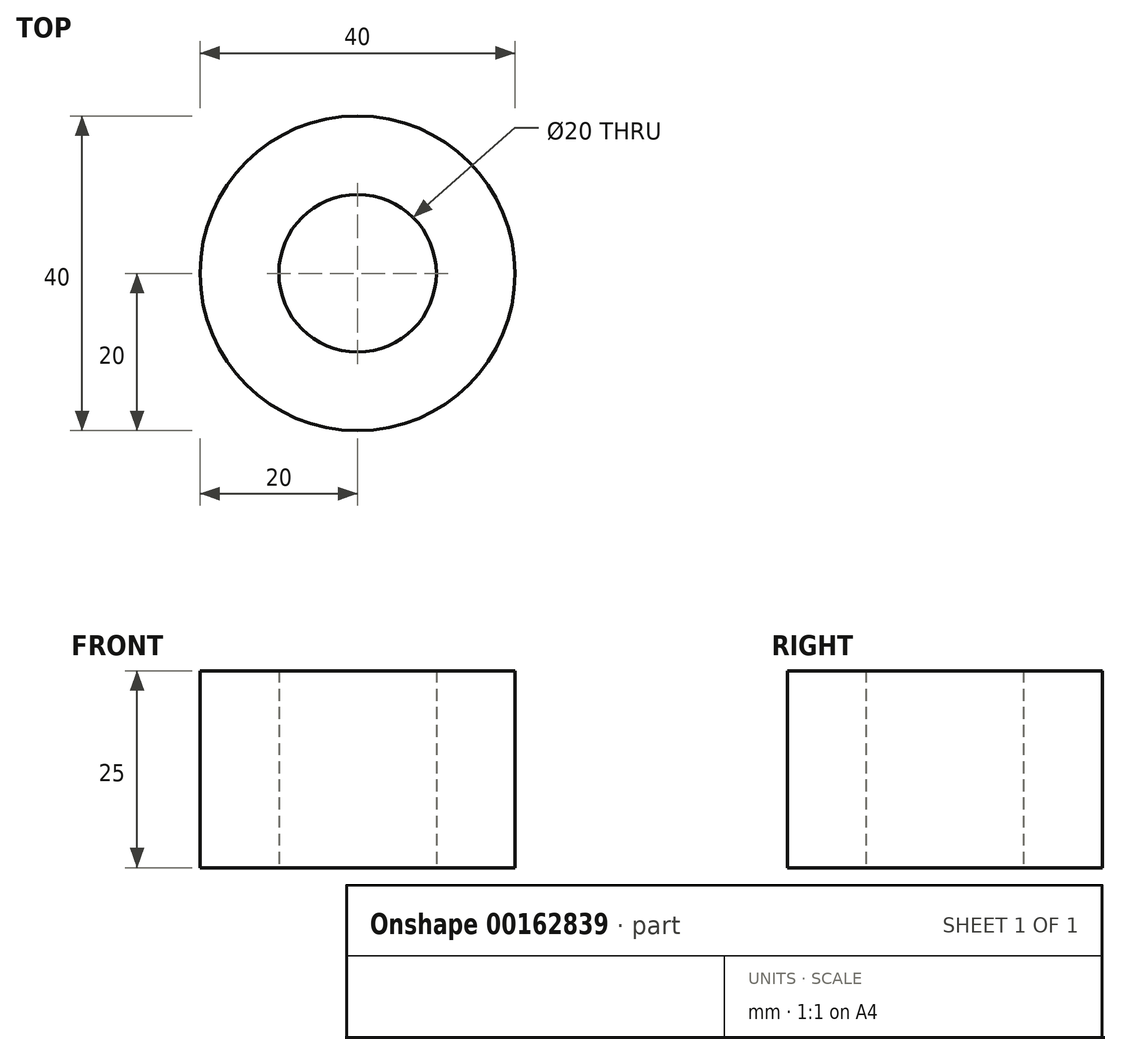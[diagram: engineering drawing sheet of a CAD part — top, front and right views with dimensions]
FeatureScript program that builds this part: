
annotation { "Feature Type Name" : "Feature", "Feature Type Description" : "" }
export const myFeature = defineFeature(function(context is Context, id is Id, definition is map)
    precondition{}
    {
        {
            var Q0;
            Q0=qCreatedBy(makeId("Top.planeOp"),FACE);
            var sketch = newSketch(context, id + "F0", { "sketchPlane" : qUnion([Q0])});
            skCircle(sketch, "E0", {"center": v(0, 0) * mm, "radius": 20 * mm});
            skCircle(sketch, "E1", {"center": v(0, 0) * mm, "radius": 10 * mm});
            skSolve(sketch);
        }
        {
            var Q0;
            Q0=makeQuery(id+"F0.imprint","IMPRINT",FACE,{"disambiguationData":[TD([[makeQuery(id+"F0.imprint","IMPRINT",EDGE,{"derivedFrom":sQuery(id+"F0.wireOp",EDGE,"E0")}),1.0]])]});
            extrude(context, id + "F1", {"entities" : qUnion([Q0]), "depth" : 25 * mm});
        }
    });
